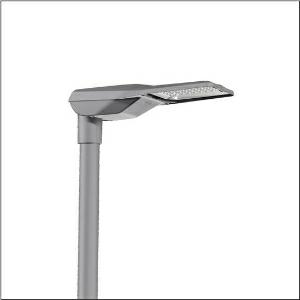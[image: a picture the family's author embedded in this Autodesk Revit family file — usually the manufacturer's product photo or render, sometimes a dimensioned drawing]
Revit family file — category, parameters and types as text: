
# Revit family: streetlight_sl_21_iq_mini___st0_5a_5xe2b41d08gb_120c
name_source: partatom
category: Lighting Fixtures
units: mm (PartAtom-declared; Revit-internal decimal feet)

## family parameters
Cut with Voids When Loaded = No
Host = Face
Light Source = No
Part Type = Normal
Room Calculation Point = No
Round Connector Dimension = Use Diameter
Shared = No

## types (1)
- --- (1 x LED, 5920 lm, 37.1 W, 4000K)
    Apparent Load = 37 VA
    CIE Flux Codes = 41 75 97 100 100
    Color Rendering = 70
    Color Temperature = 4000K
    Default Elevation = 1800 mm
    Description = Streetlight SL 21 iQ mini, mast luminaire, primary light control with lens, of PMMA, primary optical cover: cover, of toughened safety glass, transparent, light distribution: ST0.5a, light emission: direct distribution, primary light characteristic: asymmetric, installation type: post-top, side-entry, LED, High Power LED, rated luminous flux: 5.920lm, luminous efficacy: 160lm/W, light colour: 740, colour temperature: 4000K, control gear: iQ-Comfort, control: Auto-Match, Temp-Guard, Lumen-Switch, Night-Set, Smart-Wire, Light-Fading, Desk-Remote (wireless, voltage-free reading and setting of iQ features in the workshop via application-optimized NFC function/RFID function), optimised constant luminous flux control (CLO 2.0), pre-setting: linear dimming characteristic, mains connection: 220..240V, AC, 50/60Hz, start of lifetime: 37W, end of service life: 39W, reduction: 18W, luminaire housing, of diecast aluminium, powder-coated, Siteco® metallic grey (DB 702S), corrosivity category C5 mid according to DIN EN ISO 12944, please order mast flange separately, inclination adjustable: 0°, 5°, 10°, 15°, sealing non-destructively replaceable, multi-level sealing system, length: 628mm, width: 235mm, height: 110mm, mast flange for spigot size: 42mm (side-entry): 5XC10008XM4, 60/48mm (side-entry/post-top): 5XC10108XM2, 76/60mm (side-entry/post-top): 5XC10108XM1, mounting height: 4..8m, protection rating (complete): IP66, insulation class (complete): insulation class II (safety insulation), certification: CE, ENEC, ENEC+, VDE, impact resistance: IK10, permissible operating ambient temperature for outdoor applications: -40..+50°C, standard-compliant lighting for roads and squares, packaging unit: 1 piece

Light Distribution: ST0.5a
    Height = 110 mm
    Lamp = 1 x LED
    Lamp Light Flux = 5920 lm
    Lamp Power = 37.1 W
    Lamp count = 1
    Length = 625 mm
    Luminous efficacy = 160 lm/W
    Manufacturer = Siteco
    ModVariant = No
    Model = 5XE2B41D08GB
    Number of Poles = 1
    OnlyDefault = Yes
    Power Factor = 1
    Product Name = Streetlight SL 21 iQ mini | ST0.5a
    Product group = mast luminaire | pylon top
    ProductGroupID = 6100
    Protection Class = Protection class II
    Protection Degree = IP 66
    RLX_Detail_Level = 1
    RLX_Emergency_Light_Flux = 0 lm
    RLX_Emergency_Type = 0
    RLX_Emergency_Type_DB = No
    RlxData = <blob elided: 37257 chars, md5=555529af>
    Socket = socket
    Standby Power = 0 W
    System Light Flux = 5920 lm
    System Power = 37 W
    Type Comments = factory setting: luminous flux: 100 % | dim-lin: 254 | 385 mA
    Type Image = l_1003519.jpg
    URL = http://relux.com
    VarID = @adj_191336
    Voltage = 0 V
    Weight = 0.00 kg
    Width = 234 mm

## geometry (parser evidence)
native form markers: Blend x4, Sweep x10
no freeform markers — native parametric forms only
